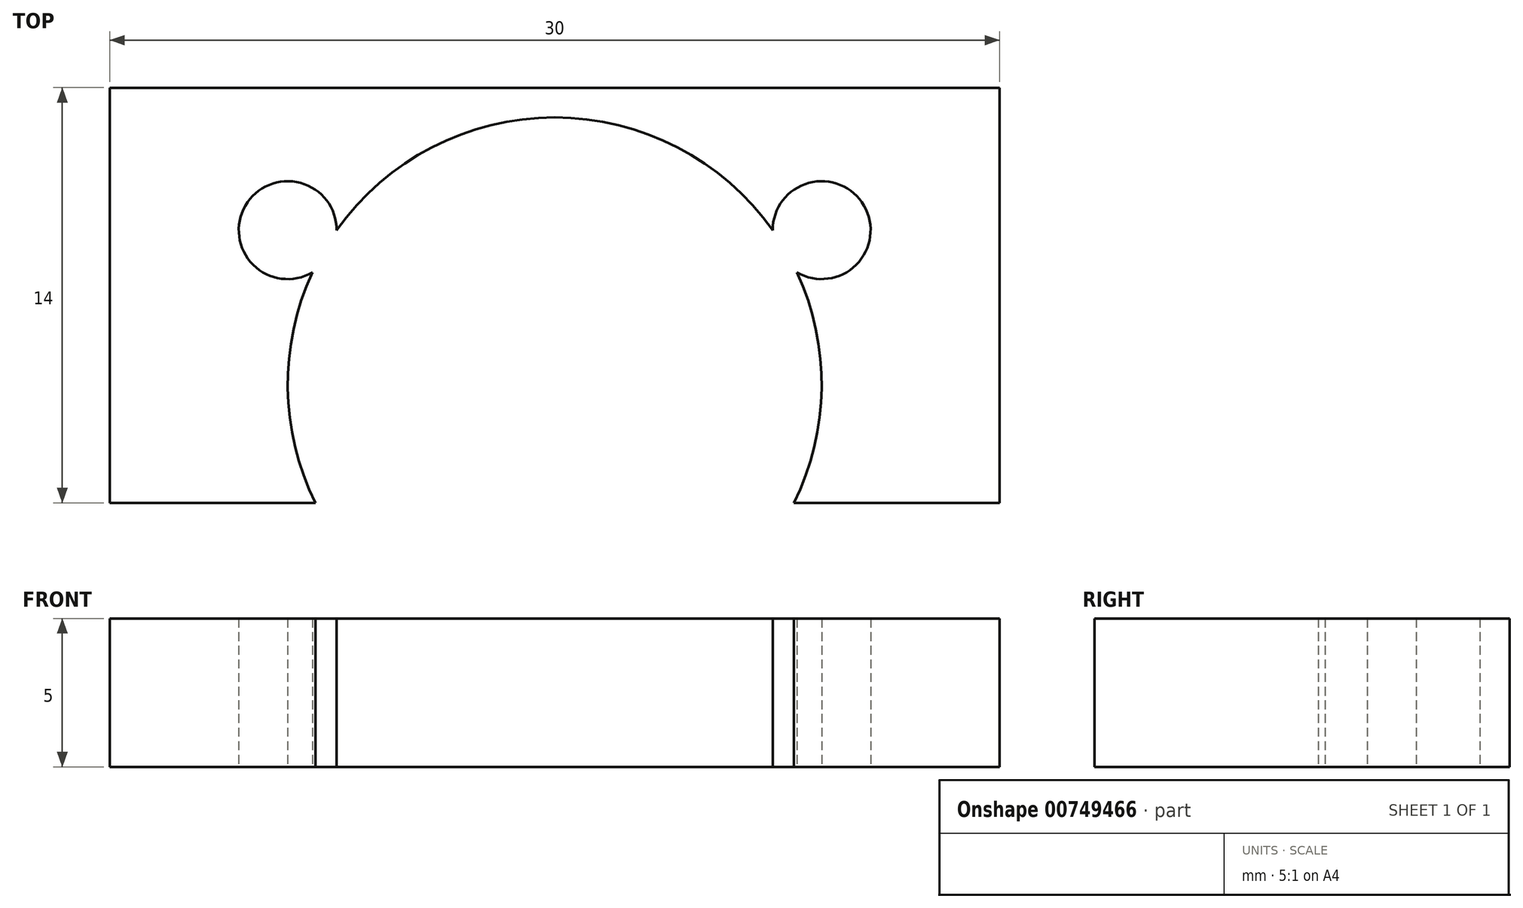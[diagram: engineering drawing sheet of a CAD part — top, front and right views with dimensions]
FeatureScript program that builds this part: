
annotation { "Feature Type Name" : "Feature", "Feature Type Description" : "" }
export const myFeature = defineFeature(function(context is Context, id is Id, definition is map)
    precondition{}
    {
        {
            var Q0;
            Q0=qCreatedBy(makeId("Top.planeOp"),FACE);
            var sketch = newSketch(context, id + "F0", { "sketchPlane" : qUnion([Q0])});
            skLineSegment(sketch, "E0.0.0", {"start": v(15, 8.49) * mm, "end": v(-15, 8.49) * mm});
            skLineSegment(sketch, "E0.0.1", {"start": v(-15, 8.49) * mm, "end": v(-15, -5.51) * mm});
            skLineSegment(sketch, "E0.0.2", {"start": v(-15, -5.51) * mm, "end": v(-10.25, -5.51) * mm});
            skFitSpline(sketch, "E0.0.3", {"points": [v(-10.25, -5.51) * mm, v(-9.52, -5.51) * mm, v(-8.8, -5.51) * mm, v(-8.06, -5.51) * mm]});
            skArc(sketch, "E0.0.4", {"start": v(-8.06, -5.51) * mm, "mid": v(-9, -1.64) * mm, "end": v(-8.17, 2.26) * mm});
            skArc(sketch, "E0.0.5", {"start": v(-7.35, 3.68) * mm, "mid": v(-10.43, 4.51) * mm, "end": v(-8.17, 2.26) * mm});
            skArc(sketch, "E0.0.6", {"start": v(-7.35, 3.68) * mm, "mid": v(0, 7.49) * mm, "end": v(7.35, 3.68) * mm});
            skArc(sketch, "E0.0.7", {"start": v(7.35, 3.68) * mm, "mid": v(10.43, 4.51) * mm, "end": v(8.17, 2.26) * mm});
            skArc(sketch, "E0.0.8", {"start": v(8.17, 2.26) * mm, "mid": v(9, -1.64) * mm, "end": v(8.06, -5.51) * mm});
            skFitSpline(sketch, "E0.0.9", {"points": [v(8.06, -5.51) * mm, v(8.8, -5.51) * mm, v(9.52, -5.51) * mm, v(10.25, -5.51) * mm]});
            skLineSegment(sketch, "E0.0.10", {"start": v(10.25, -5.51) * mm, "end": v(15, -5.51) * mm});
            skLineSegment(sketch, "E0.0.11", {"start": v(15, -5.51) * mm, "end": v(15, 8.49) * mm});
            skSolve(sketch);
        }
        {
            var Q0;
            Q0 = qSketchRegion(id + "F0", true);
            extrude(context, id + "F1", {"entities" : qUnion([Q0]), "depth" : 5 * mm, "offsetDistance" : 25 * mm});
        }
    });
